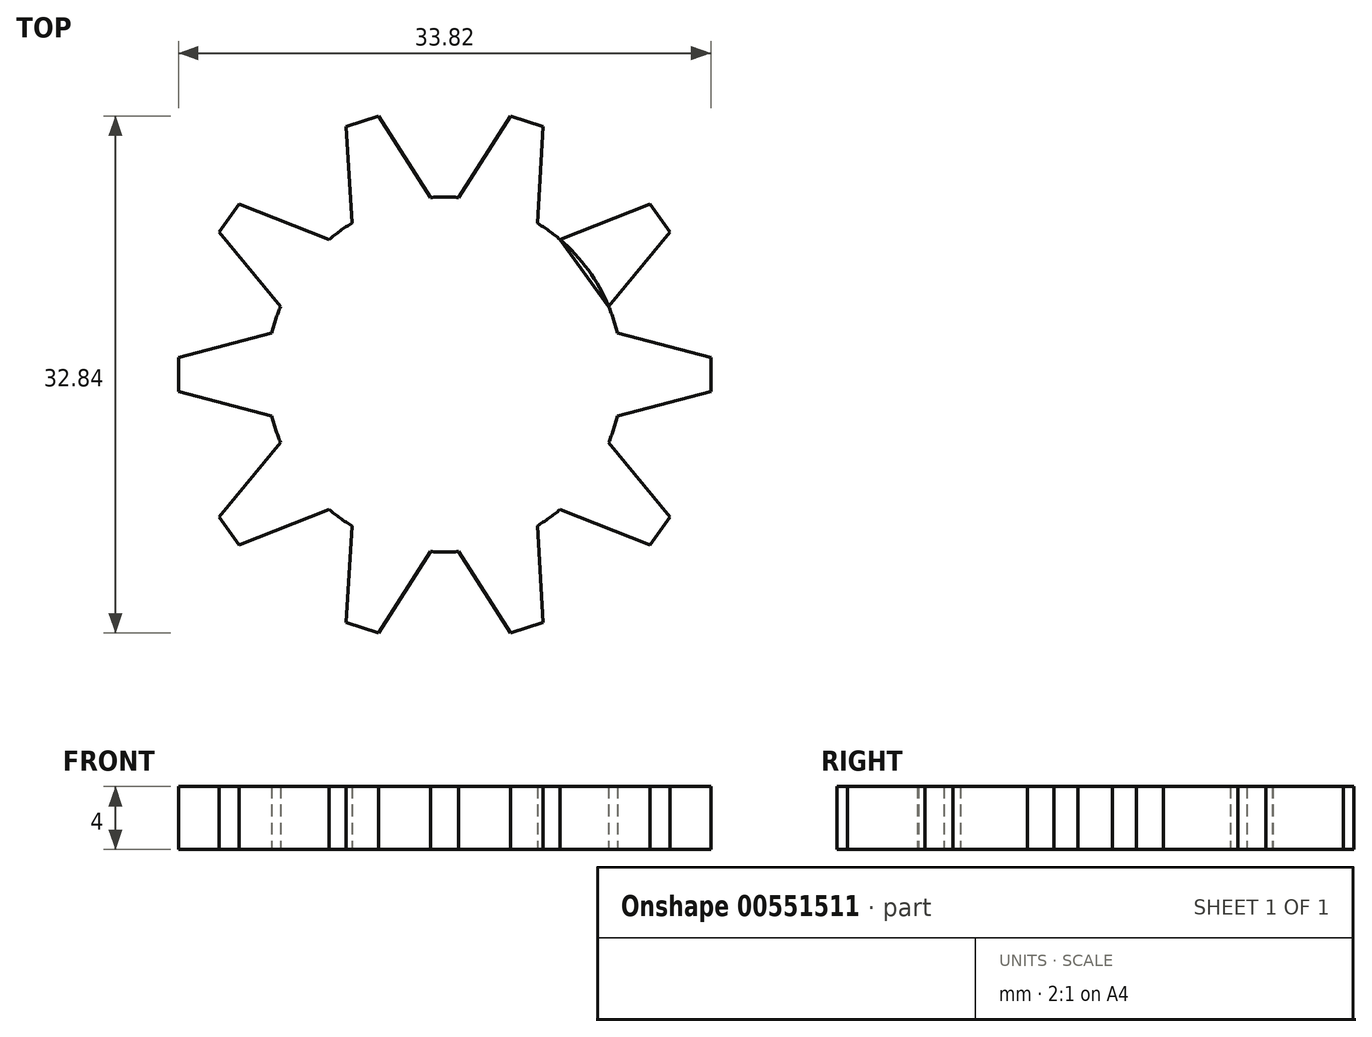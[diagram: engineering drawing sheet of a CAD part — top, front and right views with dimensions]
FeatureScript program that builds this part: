
annotation { "Feature Type Name" : "Feature", "Feature Type Description" : "" }
export const myFeature = defineFeature(function(context is Context, id is Id, definition is map)
    precondition{}
    {
        {
            var Q0;
            Q0=qCreatedBy(makeId("Top.planeOp"),FACE);
            var sketch = newSketch(context, id + "F0", { "sketchPlane" : qUnion([Q0])});
            skCircle(sketch, "E0", {"center": v(0, 0) * mm, "radius": 11.28 * mm});
            skPoint(sketch, "E1", {"position": v(0, 11.28) * mm});
            skLineSegment(sketch, "E2", {"start": v(0.9, 11.25) * mm, "end": v(4.19, 16.42) * mm});
            skLineSegment(sketch, "E3", {"start": v(4.19, 16.42) * mm, "end": v(6.26, 15.74) * mm});
            skLineSegment(sketch, "E4", {"start": v(6.26, 15.74) * mm, "end": v(5.89, 9.62) * mm});
            skLineSegment(sketch, "E5", {"start": v(7.33, 8.57) * mm, "end": v(13.04, 10.82) * mm});
            skLineSegment(sketch, "E6", {"start": v(13.04, 10.82) * mm, "end": v(14.32, 9.05) * mm});
            skLineSegment(sketch, "E7", {"start": v(14.32, 9.05) * mm, "end": v(10.42, 4.33) * mm});
            skLineSegment(sketch, "E8", {"start": v(10.97, 2.62) * mm, "end": v(16.9, 1.1) * mm});
            skLineSegment(sketch, "E9", {"start": v(16.9, 1.1) * mm, "end": v(16.9, -1.1) * mm});
            skLineSegment(sketch, "E10", {"start": v(16.9, -1.1) * mm, "end": v(10.97, -2.63) * mm});
            skLineSegment(sketch, "E11", {"start": v(10.42, -4.33) * mm, "end": v(14.32, -9.05) * mm});
            skLineSegment(sketch, "E12", {"start": v(14.32, -9.05) * mm, "end": v(13.04, -10.82) * mm});
            skLineSegment(sketch, "E13", {"start": v(13.04, -10.82) * mm, "end": v(7.33, -8.57) * mm});
            skLineSegment(sketch, "E14", {"start": v(5.89, -9.62) * mm, "end": v(6.26, -15.74) * mm});
            skLineSegment(sketch, "E15", {"start": v(6.26, -15.74) * mm, "end": v(4.19, -16.42) * mm});
            skLineSegment(sketch, "E16", {"start": v(4.19, -16.42) * mm, "end": v(0.9, -11.25) * mm});
            skPoint(sketch, "E17", {"position": v(0, -11.28) * mm});
            skLineSegment(sketch, "E18.MirrorCS", {"start": v(-16.9, 1.1) * mm, "end": v(-16.9, -1.1) * mm});
            skLineSegment(sketch, "E19.MirrorCS", {"start": v(-6.26, -15.74) * mm, "end": v(-4.19, -16.42) * mm});
            skLineSegment(sketch, "E20.MirrorCS", {"start": v(-13.04, 10.82) * mm, "end": v(-14.32, 9.05) * mm});
            skLineSegment(sketch, "E21.MirrorCS", {"start": v(-4.19, -16.42) * mm, "end": v(-0.9, -11.25) * mm});
            skLineSegment(sketch, "E22.MirrorCS", {"start": v(-13.04, -10.82) * mm, "end": v(-7.33, -8.57) * mm});
            skLineSegment(sketch, "E23.MirrorCS", {"start": v(-7.33, 8.57) * mm, "end": v(-13.04, 10.82) * mm});
            skLineSegment(sketch, "E24.MirrorCS", {"start": v(-10.42, -4.33) * mm, "end": v(-14.32, -9.05) * mm});
            skLineSegment(sketch, "E25.MirrorCS", {"start": v(-14.32, -9.05) * mm, "end": v(-13.04, -10.82) * mm});
            skLineSegment(sketch, "E26.MirrorCS", {"start": v(-16.9, -1.1) * mm, "end": v(-10.97, -2.63) * mm});
            skLineSegment(sketch, "E27.MirrorCS", {"start": v(-0.9, 11.25) * mm, "end": v(-4.19, 16.42) * mm});
            skLineSegment(sketch, "E28.MirrorCS", {"start": v(-14.32, 9.05) * mm, "end": v(-10.42, 4.33) * mm});
            skLineSegment(sketch, "E29.MirrorCS", {"start": v(-10.97, 2.62) * mm, "end": v(-16.9, 1.1) * mm});
            skLineSegment(sketch, "E30.MirrorCS", {"start": v(-4.19, 16.42) * mm, "end": v(-6.26, 15.74) * mm});
            skLineSegment(sketch, "E31.MirrorCS", {"start": v(-6.26, 15.74) * mm, "end": v(-5.89, 9.62) * mm});
            skLineSegment(sketch, "E32.MirrorCS", {"start": v(-5.89, -9.62) * mm, "end": v(-6.26, -15.74) * mm});
            skLineSegment(sketch, "E33", {"start": v(7.33, 8.57) * mm, "end": v(10.42, 4.33) * mm});
            skSolve(sketch);
        }
        {
            var Q0;
            {var subQ0=sQuery(id+"F0.wireOp",EDGE,"E11");Q0=makeQuery(id+"F0.imprint","IMPRINT",FACE,{"disambiguationData":[TD([[makeQuery(id+"F0.imprint","IMPRINT",EDGE,{"derivedFrom":subQ0}),-1.0]])]});}
            var Q1;
            {var subQ0=sQuery(id+"F0.wireOp",EDGE,"E0");var subQ8=makeQuery(id+"F0.imprint","INTERSECT",VERTEX,{"derivedFrom":[subQ0,sQuery(id+"F0.wireOp",EDGE,"E7")]});Q1=makeQuery(id+"F0.imprint","IMPRINT",FACE,{"disambiguationData":[TD([[makeQuery(id+"F0.imprint","IMPRINT",EDGE,{"disambiguationData":[TD([[subQ8,1.0]])],"derivedFrom":subQ0}),1.0]])]});}
            var Q2;
            {var subQ0=sQuery(id+"F0.wireOp",EDGE,"E8");Q2=makeQuery(id+"F0.imprint","IMPRINT",FACE,{"disambiguationData":[TD([[makeQuery(id+"F0.imprint","IMPRINT",EDGE,{"derivedFrom":subQ0}),-1.0]])]});}
            var Q3;
            {var subQ0=sQuery(id+"F0.wireOp",EDGE,"E5");Q3=makeQuery(id+"F0.imprint","IMPRINT",FACE,{"disambiguationData":[TD([[makeQuery(id+"F0.imprint","IMPRINT",EDGE,{"derivedFrom":subQ0}),-1.0]])]});}
            var Q4;
            {var subQ0=sQuery(id+"F0.wireOp",EDGE,"E2");Q4=makeQuery(id+"F0.imprint","IMPRINT",FACE,{"disambiguationData":[TD([[makeQuery(id+"F0.imprint","IMPRINT",EDGE,{"derivedFrom":subQ0}),-1.0]])]});}
            var Q5;
            {var subQ0=sQuery(id+"F0.wireOp",EDGE,"E27.MirrorCS");Q5=makeQuery(id+"F0.imprint","IMPRINT",FACE,{"disambiguationData":[TD([[makeQuery(id+"F0.imprint","IMPRINT",EDGE,{"derivedFrom":subQ0}),1.0]])]});}
            var Q6;
            {var subQ0=sQuery(id+"F0.wireOp",EDGE,"E14");Q6=makeQuery(id+"F0.imprint","IMPRINT",FACE,{"disambiguationData":[TD([[makeQuery(id+"F0.imprint","IMPRINT",EDGE,{"derivedFrom":subQ0}),-1.0]])]});}
            var Q7;
            Q7=makeQuery(id+"F0.imprint","IMPRINT",FACE,{"disambiguationData":[TD([[makeQuery(id+"F0.imprint","IMPRINT",EDGE,{"derivedFrom":sQuery(id+"F0.wireOp",EDGE,"E19.MirrorCS")}),1.0]])]});
            var Q8;
            {var subQ0=sQuery(id+"F0.wireOp",EDGE,"E22.MirrorCS");Q8=makeQuery(id+"F0.imprint","IMPRINT",FACE,{"disambiguationData":[TD([[makeQuery(id+"F0.imprint","IMPRINT",EDGE,{"derivedFrom":subQ0}),1.0]])]});}
            var Q9;
            Q9=makeQuery(id+"F0.imprint","IMPRINT",FACE,{"disambiguationData":[TD([[makeQuery(id+"F0.imprint","IMPRINT",EDGE,{"derivedFrom":sQuery(id+"F0.wireOp",EDGE,"E18.MirrorCS")}),1.0]])]});
            var Q10;
            Q10=makeQuery(id+"F0.imprint","IMPRINT",FACE,{"disambiguationData":[TD([[makeQuery(id+"F0.imprint","IMPRINT",EDGE,{"derivedFrom":sQuery(id+"F0.wireOp",EDGE,"E20.MirrorCS")}),1.0]])]});
            extrude(context, id + "F1", {"entities" : qUnion([Q0, Q1, Q2, Q3, Q4, Q5, Q6, Q7, Q8, Q9, Q10]), "depth" : 4 * mm, "offsetDistance" : 25 * mm});
        }
    });
